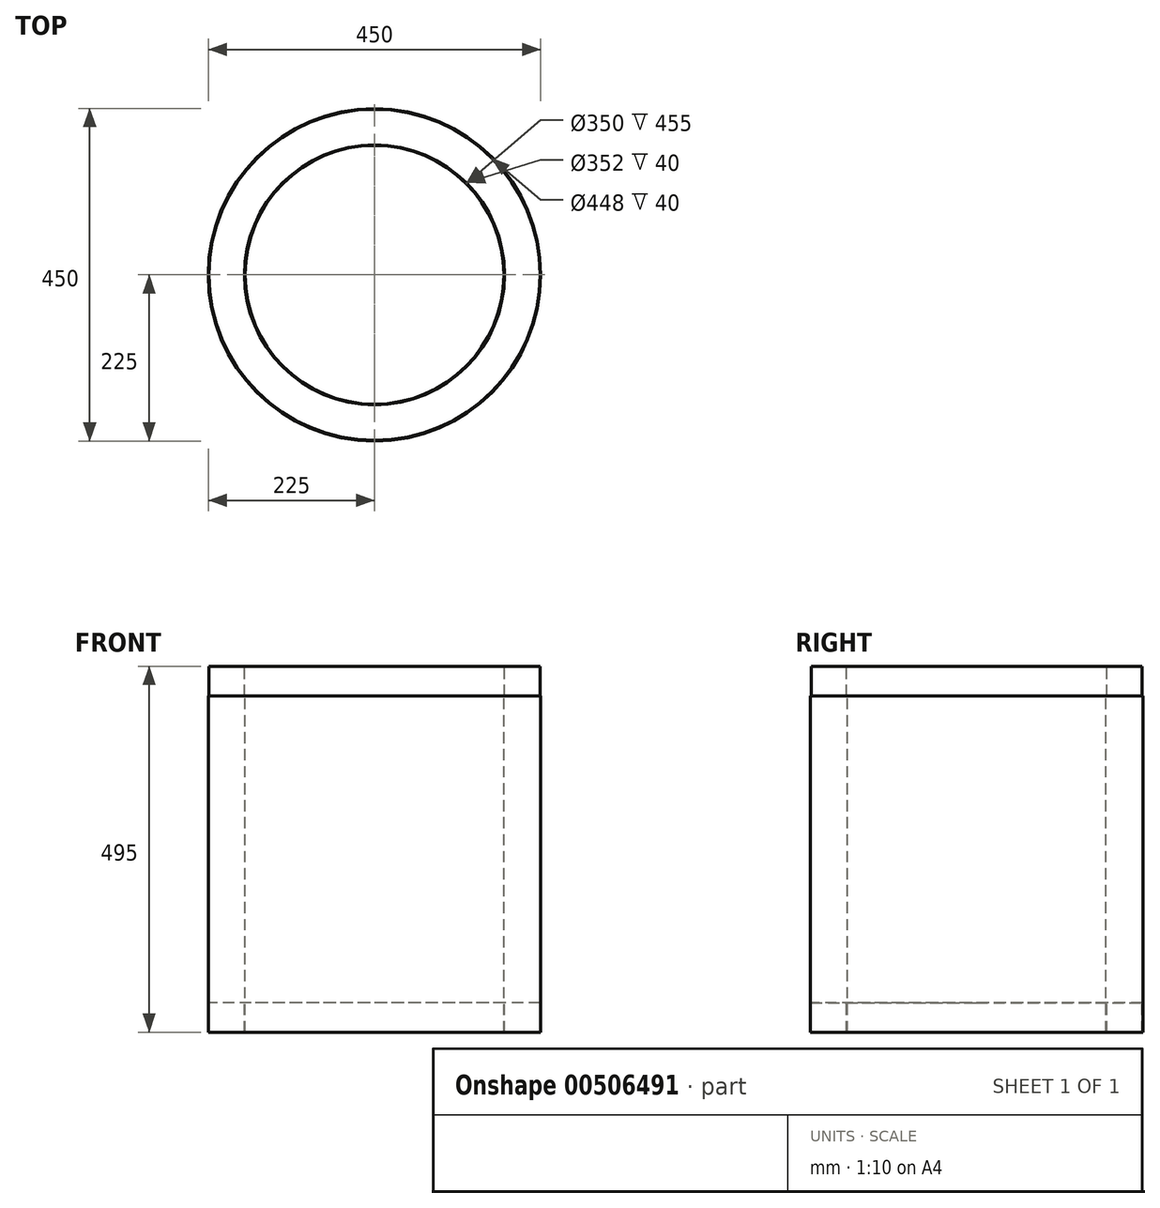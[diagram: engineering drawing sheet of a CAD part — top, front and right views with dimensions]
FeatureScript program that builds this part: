
annotation { "Feature Type Name" : "Feature", "Feature Type Description" : "" }
export const myFeature = defineFeature(function(context is Context, id is Id, definition is map)
    precondition{}
    {
        {
            var Q0;
            Q0=qCreatedBy(makeId("Front.planeOp"),FACE);
            var sketch = newSketch(context, id + "F0", { "sketchPlane" : qUnion([Q0])});
            skLineSegment(sketch, "E0", {"start": v(0, 74.87) * mm, "end": v(0, -73.71) * mm, "construction": true});
            skLineSegment(sketch, "E1", {"start": v(0, 374.84) * mm, "end": v(0, -528.94) * mm, "construction": true});
            skLineSegment(sketch, "E2", {"start": v(-175, -489.75) * mm, "end": v(-175, -34.75) * mm});
            skLineSegment(sketch, "E3", {"start": v(-175, -34.75) * mm, "end": v(-176, -34.75) * mm});
            skLineSegment(sketch, "E4", {"start": v(-176, -34.75) * mm, "end": v(-176, 5.25) * mm});
            skLineSegment(sketch, "E5", {"start": v(-176, 5.25) * mm, "end": v(-224, 5.25) * mm});
            skLineSegment(sketch, "E6", {"start": v(-224, 5.25) * mm, "end": v(-224, -34.75) * mm});
            skLineSegment(sketch, "E7", {"start": v(-224, -34.75) * mm, "end": v(-225, -34.75) * mm});
            skLineSegment(sketch, "E8", {"start": v(-225, -34.75) * mm, "end": v(-225, -489.75) * mm});
            skLineSegment(sketch, "E9", {"start": v(-225, -489.75) * mm, "end": v(-224, -489.75) * mm});
            skLineSegment(sketch, "E10", {"start": v(-224, -489.75) * mm, "end": v(-224, -449.75) * mm});
            skLineSegment(sketch, "E11", {"start": v(-224, -449.75) * mm, "end": v(-176, -449.75) * mm});
            skLineSegment(sketch, "E12", {"start": v(-176, -449.75) * mm, "end": v(-176, -489.75) * mm});
            skLineSegment(sketch, "E13", {"start": v(-176, -489.75) * mm, "end": v(-175, -489.75) * mm});
            skSolve(sketch);
        }
        {
            var Q0;
            Q0=qSketchRegion(id+"F0",true);
            var Q1;
            Q1=sQuery(id+"F0.wireOp",EDGE,"E1");
            revolve(context, id + "F1", {"entities" : qUnion([Q0]), "axis" : qUnion([Q1]), "revolveType" : RevolveType.FULL});
        }
    });
